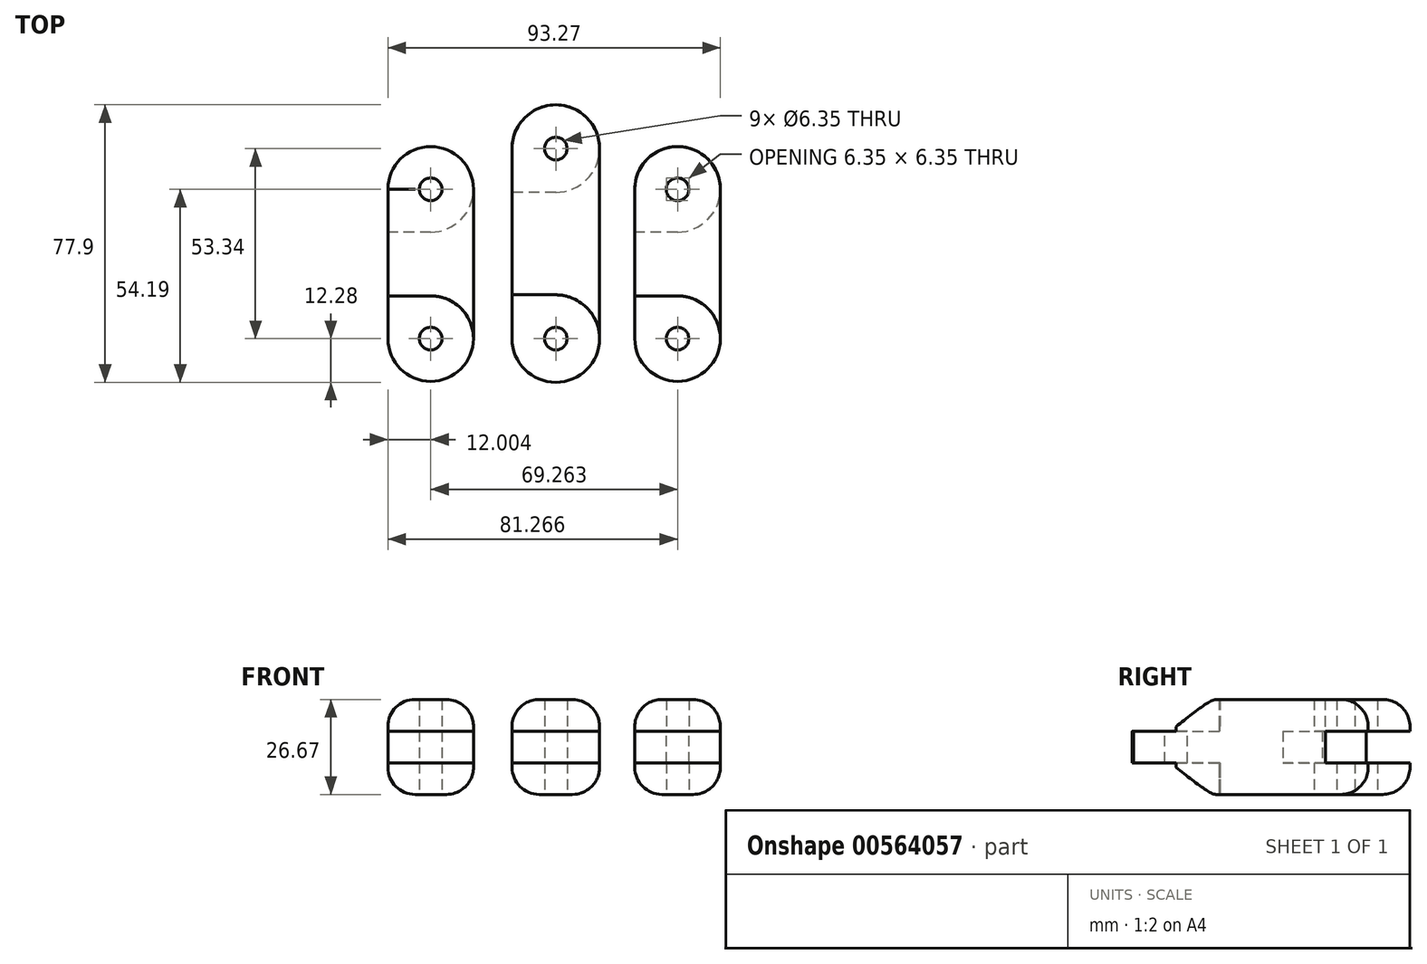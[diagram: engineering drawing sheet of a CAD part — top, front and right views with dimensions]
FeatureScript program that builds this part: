
annotation { "Feature Type Name" : "Feature", "Feature Type Description" : "" }
export const myFeature = defineFeature(function(context is Context, id is Id, definition is map)
    precondition{}
    {
        {
            var Q0;
            Q0=qCreatedBy(makeId("Top.planeOp"),FACE);
            var sketch = newSketch(context, id + "F0", { "sketchPlane" : qUnion([Q0])});
            skLineSegment(sketch, "E0", {"start": v(-47.25, 0) * mm, "end": v(-47.25, 41.91) * mm});
            skArc(sketch, "E1", {"start": v(-47.25, 0) * mm, "mid": v(-50.77, 8.49) * mm, "end": v(-59.26, 12) * mm});
            skLineSegment(sketch, "E2", {"start": v(-59.26, 12) * mm, "end": v(-71.26, 12) * mm});
            skLineSegment(sketch, "E3", {"start": v(-71.26, 41.91) * mm, "end": v(-71.26, 12) * mm});
            skArc(sketch, "E4", {"start": v(-47.25, 41.91) * mm, "mid": v(-59.26, 53.91) * mm, "end": v(-71.26, 41.91) * mm});
            skSolve(sketch);
        }
        {
            var Q0;
            Q0 = qSketchRegion(id + "F0", true);
            extrude(context, id + "F1", {"entities" : qUnion([Q0]), "depth" : 8.9 * mm, "offsetDistance" : 25.4 * mm});
        }
        {
            var Q0;
            Q0=makeQuery(id+"F1.opExtrude","CAP_FACE",FACE,{"disambiguationData":[OSD([sQuery(id+"F0.wireOp",EDGE,"E0"),sQuery(id+"F0.wireOp",EDGE,"E1"),sQuery(id+"F0.wireOp",EDGE,"E2"),sQuery(id+"F0.wireOp",EDGE,"E3"),sQuery(id+"F0.wireOp",EDGE,"E4")])],"isStart":false});
            var sketch = newSketch(context, id + "F2", { "sketchPlane" : qUnion([Q0])});
            skArc(sketch, "E5", {"start": v(-59.26, 29.9) * mm, "mid": v(-50.77, 33.42) * mm, "end": v(-47.25, 41.91) * mm});
            skLineSegment(sketch, "E6", {"start": v(-47.25, 41.91) * mm, "end": v(-47.25, 0) * mm});
            skLineSegment(sketch, "E7", {"start": v(-59.26, 29.9) * mm, "end": v(-71.26, 29.9) * mm});
            skLineSegment(sketch, "E8", {"start": v(-71.26, 29.9) * mm, "end": v(-71.26, 0) * mm});
            skArc(sketch, "E9", {"start": v(-71.26, 0) * mm, "mid": v(-59.26, -12) * mm, "end": v(-47.25, 0) * mm});
            skSolve(sketch);
        }
        {
            var Q0;
            Q0 = qSketchRegion(id + "F2", true);
            extrude(context, id + "F3", {"entities" : qUnion([Q0]), "operationType" : NewBodyOperationType.ADD, "depth" : 8.9 * mm, "offsetDistance" : 25.4 * mm});
        }
        {
            var Q0;
            Q0=makeQuery(id+"F3.opExtrude","CAP_FACE",FACE,{"disambiguationData":[OSD([sQuery(id+"F2.wireOp",EDGE,"E5"),sQuery(id+"F2.wireOp",EDGE,"E6"),sQuery(id+"F2.wireOp",EDGE,"E7"),sQuery(id+"F2.wireOp",EDGE,"E8"),sQuery(id+"F2.wireOp",EDGE,"E9")])],"isStart":false});
            var sketch = newSketch(context, id + "F4", { "sketchPlane" : qUnion([Q0])});
            skArc(sketch, "E10", {"start": v(-47.25, 0) * mm, "mid": v(-50.77, 8.49) * mm, "end": v(-59.26, 12) * mm});
            skLineSegment(sketch, "E11", {"start": v(-59.26, 12) * mm, "end": v(-71.26, 12) * mm});
            skLineSegment(sketch, "E12", {"start": v(-71.26, 12) * mm, "end": v(-71.26, 41.93) * mm});
            skLineSegment(sketch, "E13", {"start": v(-47.25, 0) * mm, "end": v(-47.25, 41.91) * mm});
            skArc(sketch, "E14", {"start": v(-47.25, 41.91) * mm, "mid": v(-59.24, 53.91) * mm, "end": v(-71.26, 41.93) * mm});
            skSolve(sketch);
        }
        {
            var Q0;
            Q0 = qSketchRegion(id + "F4", true);
            extrude(context, id + "F5", {"entities" : qUnion([Q0]), "operationType" : NewBodyOperationType.ADD, "depth" : 8.9 * mm, "offsetDistance" : 25.4 * mm});
        }
        {
            var Q0;
            Q0=sQuery(id+"F2.wireOp",VERTEX,"E5.center");
            var Q1;
            Q1=sQuery(id+"F0.wireOp",VERTEX,"E4.center");
            var Q2;
            Q2=makeQuery(id+"F1.opExtrude","SWEPT_BODY",BODY,{"disambiguationData":[OSD([sQuery(id+"F0.wireOp",EDGE,"E0"),sQuery(id+"F0.wireOp",EDGE,"E1"),sQuery(id+"F0.wireOp",EDGE,"E2"),sQuery(id+"F0.wireOp",EDGE,"E3"),sQuery(id+"F0.wireOp",EDGE,"E4")])]});
            hole(context, id + "F6", {"style" : HoleStyle.SIMPLE, "endStyle" : HoleEndStyle.THROUGH, "oppositeDirection" : true, "holeDiameter" : 6.35 * mm, "majorDiameter" : 6.35 * mm, "isTappedThrough" : true, "tappedDepth" : 12.7 * mm, "tapClearance" : 3, "locations" : qUnion([Q0, Q1]), "scope" : qUnion([Q2])});
        }
        {
            var Q0;
            Q0=sQuery(id+"F2.wireOp",VERTEX,"E9.center");
            var Q1;
            Q1=makeQuery(id+"F1.opExtrude","SWEPT_BODY",BODY,{"disambiguationData":[OSD([sQuery(id+"F0.wireOp",EDGE,"E0"),sQuery(id+"F0.wireOp",EDGE,"E1"),sQuery(id+"F0.wireOp",EDGE,"E2"),sQuery(id+"F0.wireOp",EDGE,"E3"),sQuery(id+"F0.wireOp",EDGE,"E4")])]});
            hole(context, id + "F7", {"style" : HoleStyle.SIMPLE, "endStyle" : HoleEndStyle.THROUGH, "oppositeDirection" : true, "holeDiameter" : 6.35 * mm, "majorDiameter" : 6.35 * mm, "isTappedThrough" : true, "tappedDepth" : 12.7 * mm, "tapClearance" : 3, "locations" : qUnion([Q0]), "scope" : qUnion([Q1])});
        }
        {
            var Q0;
            Q0=makeQuery(id+"F5.opExtrude","CAP_EDGE",EDGE,{"disambiguationData":[OSD([sQuery(id+"F4.wireOp",EDGE,"E13")])],"isStart":false});
            var Q1;
            Q1=makeQuery(id+"F5.opExtrude","CAP_EDGE",EDGE,{"disambiguationData":[OSD([sQuery(id+"F4.wireOp",EDGE,"E12")])],"isStart":false});
            var Q2;
            Q2=makeQuery(id+"F1.opExtrude","CAP_EDGE",EDGE,{"disambiguationData":[OSD([sQuery(id+"F0.wireOp",EDGE,"E0")])],"isStart":true});
            fillet(context, id + "F8", {"entities" : qUnion([Q0, Q1, Q2]), "radius" : 7.62 * mm, "tangentPropagation" : true, "allowEdgeOverflow" : false});
        }
        {
            var Q0;
            Q0=qCreatedBy(makeId("Top.planeOp"),FACE);
            var sketch = newSketch(context, id + "F9", { "sketchPlane" : qUnion([Q0])});
            skLineSegment(sketch, "E15", {"start": v(-11.87, 0) * mm, "end": v(-11.87, 53.34) * mm});
            skArc(sketch, "E16", {"start": v(-11.87, 53.34) * mm, "mid": v(-24.15, 65.62) * mm, "end": v(-36.43, 53.34) * mm});
            skArc(sketch, "E17", {"start": v(-11.87, 0) * mm, "mid": v(-15.47, 8.68) * mm, "end": v(-24.15, 12.28) * mm});
            skLineSegment(sketch, "E18", {"start": v(-24.15, 12.28) * mm, "end": v(-36.43, 12.28) * mm});
            skLineSegment(sketch, "E19", {"start": v(-36.43, 53.34) * mm, "end": v(-36.43, 12.28) * mm});
            skSolve(sketch);
        }
        {
            var Q0;
            Q0 = qSketchRegion(id + "F9", true);
            extrude(context, id + "F10", {"entities" : qUnion([Q0]), "depth" : 8.9 * mm, "offsetDistance" : 25.4 * mm});
        }
        {
            var Q0;
            Q0=makeQuery(id+"F10.opExtrude","CAP_FACE",FACE,{"disambiguationData":[OSD([sQuery(id+"F9.wireOp",EDGE,"E15"),sQuery(id+"F9.wireOp",EDGE,"E16"),sQuery(id+"F9.wireOp",EDGE,"E17"),sQuery(id+"F9.wireOp",EDGE,"E18"),sQuery(id+"F9.wireOp",EDGE,"E19")])],"isStart":false});
            var sketch = newSketch(context, id + "F11", { "sketchPlane" : qUnion([Q0])});
            skArc(sketch, "E20", {"start": v(-24.15, 41.06) * mm, "mid": v(-15.47, 44.66) * mm, "end": v(-11.87, 53.34) * mm});
            skLineSegment(sketch, "E21", {"start": v(-24.15, 41.06) * mm, "end": v(-36.43, 41.06) * mm});
            skLineSegment(sketch, "E22", {"start": v(-36.43, 41.06) * mm, "end": v(-36.43, 0) * mm});
            skLineSegment(sketch, "E23", {"start": v(-11.87, 53.34) * mm, "end": v(-11.87, 0) * mm});
            skArc(sketch, "E24", {"start": v(-36.43, 0) * mm, "mid": v(-24.15, -12.28) * mm, "end": v(-11.87, 0) * mm});
            skSolve(sketch);
        }
        {
            var Q0;
            Q0 = qSketchRegion(id + "F11", true);
            extrude(context, id + "F12", {"entities" : qUnion([Q0]), "operationType" : NewBodyOperationType.ADD, "depth" : 8.9 * mm, "offsetDistance" : 25.4 * mm});
        }
        {
            var Q0;
            Q0=makeQuery(id+"F12.opExtrude","CAP_FACE",FACE,{"disambiguationData":[OSD([sQuery(id+"F11.wireOp",EDGE,"E20"),sQuery(id+"F11.wireOp",EDGE,"E21"),sQuery(id+"F11.wireOp",EDGE,"E22"),sQuery(id+"F11.wireOp",EDGE,"E23"),sQuery(id+"F11.wireOp",EDGE,"E24")])],"isStart":false});
            var sketch = newSketch(context, id + "F13", { "sketchPlane" : qUnion([Q0])});
            skLineSegment(sketch, "E25", {"start": v(-11.87, 53.34) * mm, "end": v(-11.87, 0) * mm});
            skArc(sketch, "E26", {"start": v(-11.87, 53.34) * mm, "mid": v(-24.15, 65.62) * mm, "end": v(-36.43, 53.34) * mm});
            skArc(sketch, "E27", {"start": v(-11.87, 0) * mm, "mid": v(-15.47, 8.68) * mm, "end": v(-24.15, 12.28) * mm});
            skLineSegment(sketch, "E28", {"start": v(-24.15, 12.28) * mm, "end": v(-36.43, 12.28) * mm});
            skLineSegment(sketch, "E29", {"start": v(-36.43, 53.34) * mm, "end": v(-36.43, 12.28) * mm});
            skSolve(sketch);
        }
        {
            var Q0;
            Q0 = qSketchRegion(id + "F13", true);
            extrude(context, id + "F14", {"entities" : qUnion([Q0]), "operationType" : NewBodyOperationType.ADD, "depth" : 8.9 * mm, "offsetDistance" : 25.4 * mm});
        }
        {
            var Q0;
            Q0=sQuery(id+"F11.wireOp",VERTEX,"E24.center");
            var Q1;
            Q1=makeQuery(id+"F10.opExtrude","SWEPT_BODY",BODY,{"disambiguationData":[OSD([sQuery(id+"F9.wireOp",EDGE,"E15"),sQuery(id+"F9.wireOp",EDGE,"E16"),sQuery(id+"F9.wireOp",EDGE,"E17"),sQuery(id+"F9.wireOp",EDGE,"E18"),sQuery(id+"F9.wireOp",EDGE,"E19")])]});
            hole(context, id + "F15", {"style" : HoleStyle.SIMPLE, "endStyle" : HoleEndStyle.THROUGH, "oppositeDirection" : true, "holeDiameter" : 6.35 * mm, "majorDiameter" : 6.35 * mm, "isTappedThrough" : true, "tappedDepth" : 12.7 * mm, "tapClearance" : 3, "locations" : qUnion([Q0]), "scope" : qUnion([Q1])});
        }
        {
            var Q0;
            Q0=sQuery(id+"F9.wireOp",VERTEX,"E16.center");
            var Q1;
            Q1=makeQuery(id+"F10.opExtrude","SWEPT_BODY",BODY,{"disambiguationData":[OSD([sQuery(id+"F9.wireOp",EDGE,"E15"),sQuery(id+"F9.wireOp",EDGE,"E16"),sQuery(id+"F9.wireOp",EDGE,"E17"),sQuery(id+"F9.wireOp",EDGE,"E18"),sQuery(id+"F9.wireOp",EDGE,"E19")])]});
            hole(context, id + "F16", {"style" : HoleStyle.SIMPLE, "endStyle" : HoleEndStyle.THROUGH, "oppositeDirection" : true, "holeDiameter" : 6.35 * mm, "majorDiameter" : 6.35 * mm, "isTappedThrough" : true, "tappedDepth" : 12.7 * mm, "tapClearance" : 3, "locations" : qUnion([Q0]), "scope" : qUnion([Q1])});
        }
        {
            var Q0;
            Q0=makeQuery(id+"F10.opExtrude","CAP_EDGE",EDGE,{"disambiguationData":[OSD([sQuery(id+"F9.wireOp",EDGE,"E19")])],"isStart":true});
            var Q1;
            Q1=makeQuery(id+"F14.opExtrude","CAP_EDGE",EDGE,{"disambiguationData":[OSD([sQuery(id+"F13.wireOp",EDGE,"E25")])],"isStart":false});
            fillet(context, id + "F17", {"entities" : qUnion([Q0, Q1]), "radius" : 7.62 * mm, "tangentPropagation" : true, "allowEdgeOverflow" : false});
        }
        {
            var Q0;
            Q0=qCreatedBy(makeId("Top.planeOp"),FACE);
            var sketch = newSketch(context, id + "F18", { "sketchPlane" : qUnion([Q0])});
            skLineSegment(sketch, "E30", {"start": v(22, 0) * mm, "end": v(22, 41.91) * mm});
            skArc(sketch, "E31", {"start": v(22, 41.91) * mm, "mid": v(10, 53.91) * mm, "end": v(-2, 41.91) * mm});
            skArc(sketch, "E32", {"start": v(22, 0) * mm, "mid": v(18.5, 8.49) * mm, "end": v(10, 12) * mm});
            skLineSegment(sketch, "E33", {"start": v(10, 12) * mm, "end": v(-2, 12) * mm});
            skLineSegment(sketch, "E34", {"start": v(-2, 41.91) * mm, "end": v(-2, 12) * mm});
            skSolve(sketch);
        }
        {
            var Q0;
            Q0 = qSketchRegion(id + "F18", true);
            extrude(context, id + "F19", {"entities" : qUnion([Q0]), "depth" : 8.9 * mm, "offsetDistance" : 25.4 * mm});
        }
        {
            var Q0;
            Q0=makeQuery(id+"F19.opExtrude","CAP_FACE",FACE,{"disambiguationData":[OSD([sQuery(id+"F18.wireOp",EDGE,"E30"),sQuery(id+"F18.wireOp",EDGE,"E31"),sQuery(id+"F18.wireOp",EDGE,"E32"),sQuery(id+"F18.wireOp",EDGE,"E33"),sQuery(id+"F18.wireOp",EDGE,"E34")])],"isStart":false});
            var sketch = newSketch(context, id + "F20", { "sketchPlane" : qUnion([Q0])});
            skLineSegment(sketch, "E35", {"start": v(22, 41.91) * mm, "end": v(22, 0) * mm});
            skArc(sketch, "E36", {"start": v(10, 29.9) * mm, "mid": v(18.5, 33.42) * mm, "end": v(22, 41.91) * mm});
            skLineSegment(sketch, "E37", {"start": v(10, 29.9) * mm, "end": v(-2, 29.9) * mm});
            skLineSegment(sketch, "E38", {"start": v(-2, 29.9) * mm, "end": v(-2, 0) * mm});
            skArc(sketch, "E39", {"start": v(-2, 0) * mm, "mid": v(10, -12) * mm, "end": v(22, 0) * mm});
            skSolve(sketch);
        }
        {
            var Q0;
            Q0 = qSketchRegion(id + "F20", true);
            extrude(context, id + "F21", {"entities" : qUnion([Q0]), "operationType" : NewBodyOperationType.ADD, "depth" : 8.9 * mm, "offsetDistance" : 25.4 * mm});
        }
        {
            var Q0;
            Q0=makeQuery(id+"F21.opExtrude","CAP_FACE",FACE,{"disambiguationData":[OSD([sQuery(id+"F20.wireOp",EDGE,"E35"),sQuery(id+"F20.wireOp",EDGE,"E36"),sQuery(id+"F20.wireOp",EDGE,"E37"),sQuery(id+"F20.wireOp",EDGE,"E38"),sQuery(id+"F20.wireOp",EDGE,"E39")])],"isStart":false});
            var sketch = newSketch(context, id + "F22", { "sketchPlane" : qUnion([Q0])});
            skLineSegment(sketch, "E40", {"start": v(22, 41.91) * mm, "end": v(22, 0) * mm});
            skArc(sketch, "E41", {"start": v(22, 41.91) * mm, "mid": v(10, 53.91) * mm, "end": v(-2, 41.9) * mm});
            skArc(sketch, "E42", {"start": v(22, 0) * mm, "mid": v(18.5, 8.49) * mm, "end": v(10, 12) * mm});
            skLineSegment(sketch, "E43", {"start": v(10, 12) * mm, "end": v(-2, 12) * mm});
            skLineSegment(sketch, "E44", {"start": v(-2, 41.9) * mm, "end": v(-2, 12) * mm});
            skSolve(sketch);
        }
        {
            var Q0;
            Q0 = qSketchRegion(id + "F22", true);
            extrude(context, id + "F23", {"entities" : qUnion([Q0]), "operationType" : NewBodyOperationType.ADD, "depth" : 8.9 * mm, "offsetDistance" : 25.4 * mm});
        }
        {
            var Q0;
            Q0=sQuery(id+"F22.wireOp",VERTEX,"E42.center");
            var Q1;
            Q1=makeQuery(id+"F19.opExtrude","SWEPT_BODY",BODY,{"disambiguationData":[OSD([sQuery(id+"F18.wireOp",EDGE,"E30"),sQuery(id+"F18.wireOp",EDGE,"E31"),sQuery(id+"F18.wireOp",EDGE,"E32"),sQuery(id+"F18.wireOp",EDGE,"E33"),sQuery(id+"F18.wireOp",EDGE,"E34")])]});
            hole(context, id + "F24", {"style" : HoleStyle.SIMPLE, "endStyle" : HoleEndStyle.THROUGH, "holeDiameter" : 6.35 * mm, "majorDiameter" : 6.35 * mm, "isTappedThrough" : true, "tappedDepth" : 12.7 * mm, "tapClearance" : 3, "locations" : qUnion([Q0]), "scope" : qUnion([Q1])});
        }
        {
            var Q0;
            Q0=sQuery(id+"F22.wireOp",VERTEX,"E41.center");
            var Q1;
            Q1=makeQuery(id+"F19.opExtrude","SWEPT_BODY",BODY,{"disambiguationData":[OSD([sQuery(id+"F18.wireOp",EDGE,"E30"),sQuery(id+"F18.wireOp",EDGE,"E31"),sQuery(id+"F18.wireOp",EDGE,"E32"),sQuery(id+"F18.wireOp",EDGE,"E33"),sQuery(id+"F18.wireOp",EDGE,"E34")])]});
            hole(context, id + "F25", {"style" : HoleStyle.SIMPLE, "endStyle" : HoleEndStyle.THROUGH, "oppositeDirection" : true, "holeDiameter" : 6.35 * mm, "majorDiameter" : 6.35 * mm, "isTappedThrough" : true, "tappedDepth" : 12.7 * mm, "tapClearance" : 3, "locations" : qUnion([Q0]), "scope" : qUnion([Q1])});
        }
        {
            var Q0;
            Q0=makeQuery(id+"F23.opExtrude","CAP_EDGE",EDGE,{"disambiguationData":[OSD([sQuery(id+"F22.wireOp",EDGE,"E40")])],"isStart":false});
            var Q1;
            Q1=makeQuery(id+"F19.opExtrude","CAP_EDGE",EDGE,{"disambiguationData":[OSD([sQuery(id+"F18.wireOp",EDGE,"E30")])],"isStart":true});
            fillet(context, id + "F26", {"entities" : qUnion([Q0, Q1]), "radius" : 7.62 * mm, "tangentPropagation" : true, "allowEdgeOverflow" : false});
        }
        {
            var Q0;
            Q0=sQuery(id+"F18.wireOp",VERTEX,"E31.center");
            var Q1;
            Q1=makeQuery(id+"F19.opExtrude","SWEPT_BODY",BODY,{"disambiguationData":[OSD([sQuery(id+"F18.wireOp",EDGE,"E30"),sQuery(id+"F18.wireOp",EDGE,"E31"),sQuery(id+"F18.wireOp",EDGE,"E32"),sQuery(id+"F18.wireOp",EDGE,"E33"),sQuery(id+"F18.wireOp",EDGE,"E34")])]});
            hole(context, id + "F27", {"style" : HoleStyle.SIMPLE, "endStyle" : HoleEndStyle.THROUGH, "oppositeDirection" : true, "holeDiameter" : 6.35 * mm, "majorDiameter" : 6.35 * mm, "isTappedThrough" : true, "tappedDepth" : 12.7 * mm, "tapClearance" : 3, "locations" : qUnion([Q0]), "scope" : qUnion([Q1])});
        }
    });
